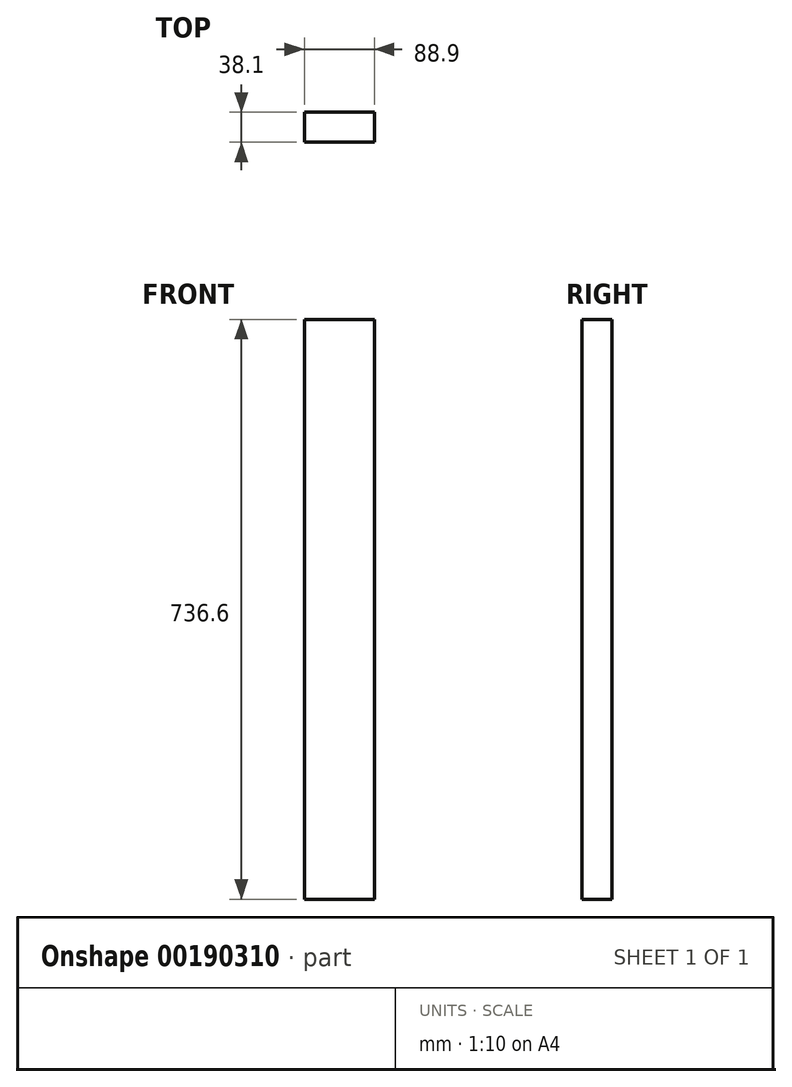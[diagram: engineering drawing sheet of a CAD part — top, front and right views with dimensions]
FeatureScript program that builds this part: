
annotation { "Feature Type Name" : "Feature", "Feature Type Description" : "" }
export const myFeature = defineFeature(function(context is Context, id is Id, definition is map)
    precondition{}
    {
        {
            var Q0;
            Q0=qCreatedBy(makeId("Top.planeOp"),FACE);
            var sketch = newSketch(context, id + "F0", { "sketchPlane" : qUnion([Q0])});
            skLineSegment(sketch, "E0.bottom", {"start": v(44.45, -19.05) * mm, "end": v(-44.45, -19.05) * mm});
            skLineSegment(sketch, "E0.top", {"start": v(44.45, 19.05) * mm, "end": v(-44.45, 19.05) * mm});
            skLineSegment(sketch, "E0.left", {"start": v(44.45, -19.05) * mm, "end": v(44.45, 19.05) * mm});
            skLineSegment(sketch, "E0.right", {"start": v(-44.45, -19.05) * mm, "end": v(-44.45, 19.05) * mm});
            skPoint(sketch, "E0.middle", {"position": v(0, 0) * mm});
            skSolve(sketch);
        }
        {
            var Q0;
            Q0=makeQuery(id+"F0.imprint","IMPRINT",FACE,{"disambiguationData":[TD([[makeQuery(id+"F0.imprint","IMPRINT",EDGE,{"derivedFrom":sQuery(id+"F0.wireOp",EDGE,"E0.bottom")}),-1.0]])]});
            extrude(context, id + "F1", {"entities" : qUnion([Q0]), "depth" : 736.6 * mm});
        }
    });
